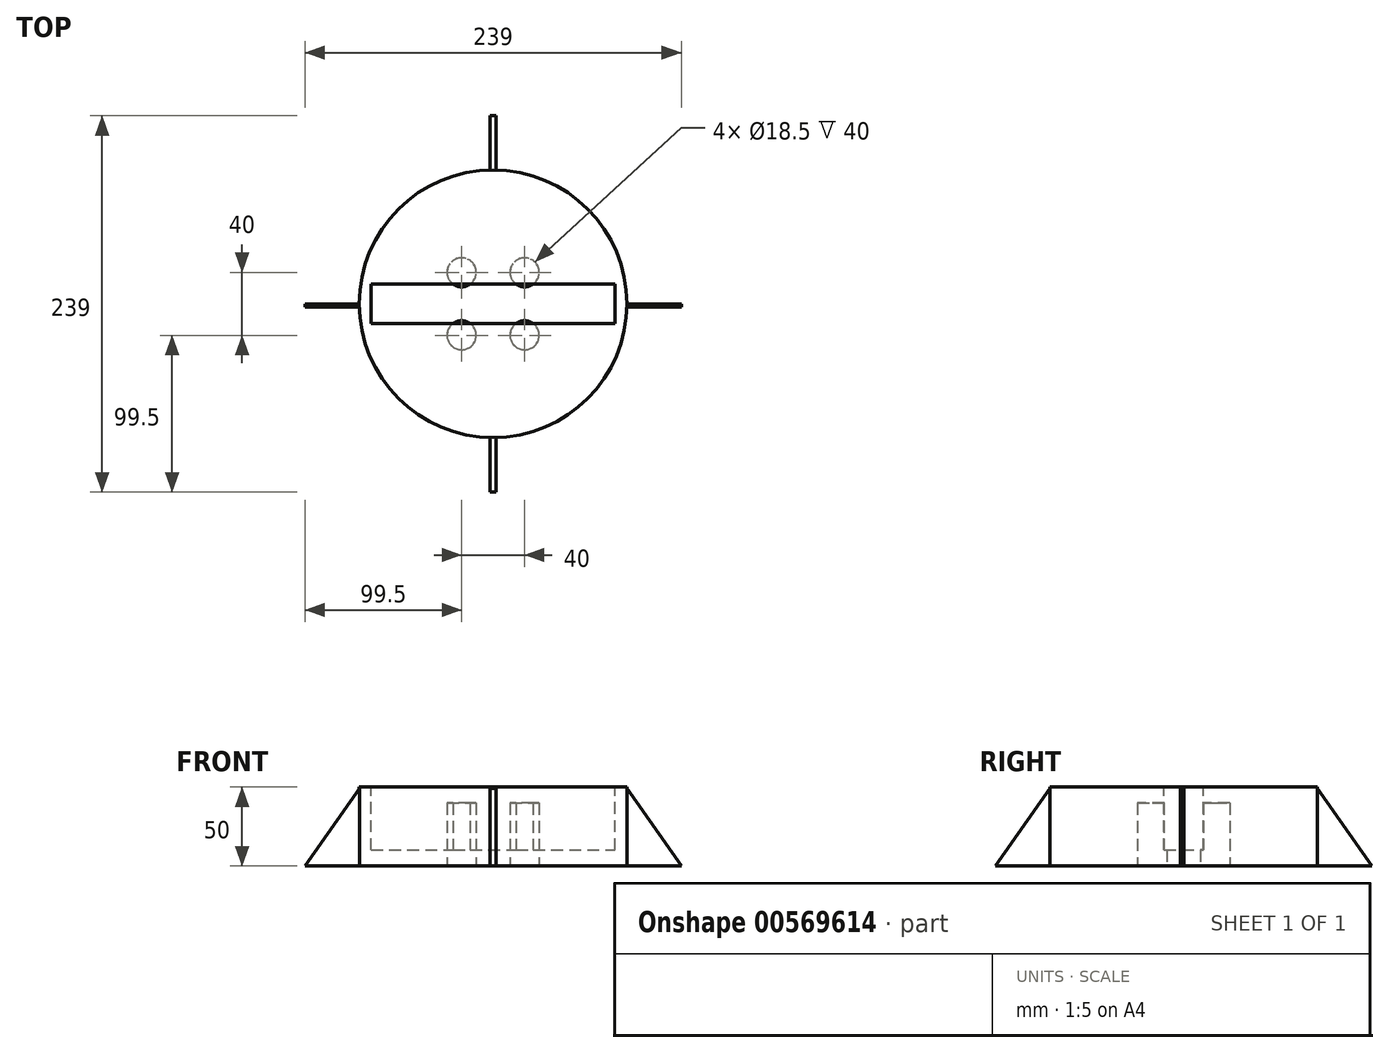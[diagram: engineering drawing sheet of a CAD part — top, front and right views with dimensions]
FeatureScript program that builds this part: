
annotation { "Feature Type Name" : "Feature", "Feature Type Description" : "" }
export const myFeature = defineFeature(function(context is Context, id is Id, definition is map)
    precondition{}
    {
        {
            var Q0;
            Q0=qCreatedBy(makeId("Top.planeOp"),FACE);
            var sketch = newSketch(context, id + "F0", { "sketchPlane" : qUnion([Q0])});
            skCircle(sketch, "E0", {"center": v(0, 0) * mm, "radius": 85 * mm});
            skSolve(sketch);
        }
        {
            var Q0;
            Q0 = qSketchRegion(id + "F0", true);
            extrude(context, id + "F1", {"entities" : qUnion([Q0]), "depth" : 50 * mm, "offsetDistance" : 25 * mm});
        }
        {
            var Q0;
            Q0=makeQuery(id+"F1.opExtrude","CAP_FACE",FACE,{"disambiguationData":[OSD([sQuery(id+"F0.wireOp",EDGE,"E0")])],"isStart":true});
            var sketch = newSketch(context, id + "F2", { "sketchPlane" : qUnion([Q0])});
            skCircle(sketch, "E1", {"center": v(20, 20) * mm, "radius": 9.25 * mm});
            skCircle(sketch, "E2", {"center": v(-20, 20) * mm, "radius": 9.25 * mm});
            skCircle(sketch, "E3", {"center": v(-20, -20) * mm, "radius": 9.25 * mm});
            skCircle(sketch, "E4", {"center": v(20, -20) * mm, "radius": 9.25 * mm});
            skSolve(sketch);
        }
        {
            var Q0;
            Q0 = qSketchRegion(id + "F2", true);
            extrude(context, id + "F3", {"entities" : qUnion([Q0]), "operationType" : NewBodyOperationType.REMOVE, "oppositeDirection" : true, "depth" : 40 * mm, "offsetDistance" : 25 * mm});
        }
        {
            var Q0;
            Q0=makeQuery(id+"F1.opExtrude","CAP_FACE",FACE,{"disambiguationData":[OSD([sQuery(id+"F0.wireOp",EDGE,"E0")])],"isStart":false});
            var sketch = newSketch(context, id + "F4", { "sketchPlane" : qUnion([Q0])});
            skLineSegment(sketch, "E5.bottom", {"start": v(-77.5, -12.5) * mm, "end": v(77.5, -12.5) * mm});
            skLineSegment(sketch, "E5.top", {"start": v(-77.5, 12.5) * mm, "end": v(77.5, 12.5) * mm});
            skLineSegment(sketch, "E5.left", {"start": v(-77.5, -12.5) * mm, "end": v(-77.5, 12.5) * mm});
            skLineSegment(sketch, "E5.right", {"start": v(77.5, -12.5) * mm, "end": v(77.5, 12.5) * mm});
            skSolve(sketch);
        }
        {
            var Q0;
            Q0 = qSketchRegion(id + "F4", true);
            extrude(context, id + "F5", {"entities" : qUnion([Q0]), "operationType" : NewBodyOperationType.REMOVE, "oppositeDirection" : true, "depth" : 40 * mm, "offsetDistance" : 25 * mm});
        }
        {
            var Q0;
            Q0=qCreatedBy(makeId("Right.planeOp"),FACE);
            var sketch = newSketch(context, id + "F6", { "sketchPlane" : qUnion([Q0])});
            skLineSegment(sketch, "E6", {"start": v(-84.5, 0) * mm, "end": v(-84.5, 50) * mm});
            skLineSegment(sketch, "E7", {"start": v(-84.5, 50) * mm, "end": v(-119.5, 0) * mm});
            skLineSegment(sketch, "E8", {"start": v(-119.5, 0) * mm, "end": v(-84.5, 0) * mm});
            skSolve(sketch);
        }
        {
            var Q0;
            Q0 = qSketchRegion(id + "F6", true);
            extrude(context, id + "F7", {"entities" : qUnion([Q0]), "operationType" : NewBodyOperationType.ADD, "depth" : 2 * mm, "offsetDistance" : 25 * mm});
        }
        {
            var Q0;
            Q0=makeQuery(id+"F1.opExtrude","SWEPT_BODY",BODY,{"disambiguationData":[OSD([sQuery(id+"F0.wireOp",EDGE,"E0")])]});
            var Q1;
            Q1=qCreatedBy(makeId("Front.planeOp"),FACE);
            mirror(context, id + "F8", {"operationType" : NewBodyOperationType.ADD, "entities" : qUnion([Q0]), "mirrorPlane" : qUnion([Q1])});
        }
        {
            var Q0;
            Q0=qCreatedBy(makeId("Front.planeOp"),FACE);
            var sketch = newSketch(context, id + "F9", { "sketchPlane" : qUnion([Q0])});
            skLineSegment(sketch, "E9", {"start": v(-84.5, 50) * mm, "end": v(-84.5, 0) * mm});
            skLineSegment(sketch, "E10", {"start": v(-84.5, 0) * mm, "end": v(-119.5, 0) * mm});
            skLineSegment(sketch, "E11", {"start": v(-119.5, 0) * mm, "end": v(-84.5, 50) * mm});
            skSolve(sketch);
        }
        {
            var Q0;
            Q0 = qSketchRegion(id + "F9", true);
            extrude(context, id + "F10", {"entities" : qUnion([Q0]), "operationType" : NewBodyOperationType.ADD, "depth" : 2 * mm, "offsetDistance" : 25 * mm});
        }
        {
            var Q0;
            Q0=makeQuery(id+"F1.opExtrude","SWEPT_BODY",BODY,{"disambiguationData":[OSD([sQuery(id+"F0.wireOp",EDGE,"E0")])]});
            var Q1;
            Q1=qCreatedBy(makeId("Right.planeOp"),FACE);
            mirror(context, id + "F11", {"operationType" : NewBodyOperationType.ADD, "entities" : qUnion([Q0]), "mirrorPlane" : qUnion([Q1])});
        }
    });
